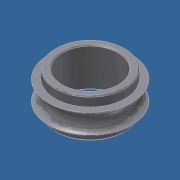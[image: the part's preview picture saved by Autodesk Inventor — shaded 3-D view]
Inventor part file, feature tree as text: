
AUTODESK INVENTOR PART (.ipt)
format: ipt  version: unknown  size: 255,488 bytes
history: native  units: in
note: dims shown in document units (in); Inventor stores cm internally (conversion verified against a paired STEP export)
features: chamfer x2, revolve x1, sketch x1
ambient origin geometry x8: Origin, YZ Plane, XZ Plane, XY Plane, X Axis, Y Axis, Z Axis, Center Point
bodies: Solid1 (feature_tree)
feature tree (4):
  revolve  "Revolution1"  [1 undecoded]
  chamfer  "Chamfer1"  Distance=0.063in
  chamfer  "Chamfer2"  Distance=0.18in
  sketch  "Sketch1"  dims[d0=0.0856in d2=0.0856in d3=0.063in d7=0.18in d8=0.003in d9=90.0deg d10=0.01in d11=0.125in d12=45.0deg d13=0.01in d14=0.125in d15=45.0deg d16=0.25in d17=0.4065in]
note: 1 required parameter value undecoded (feature->parameter linkage not recoverable at this tier; creation-order binding heuristic only, values carry confidence <= 0.55)
